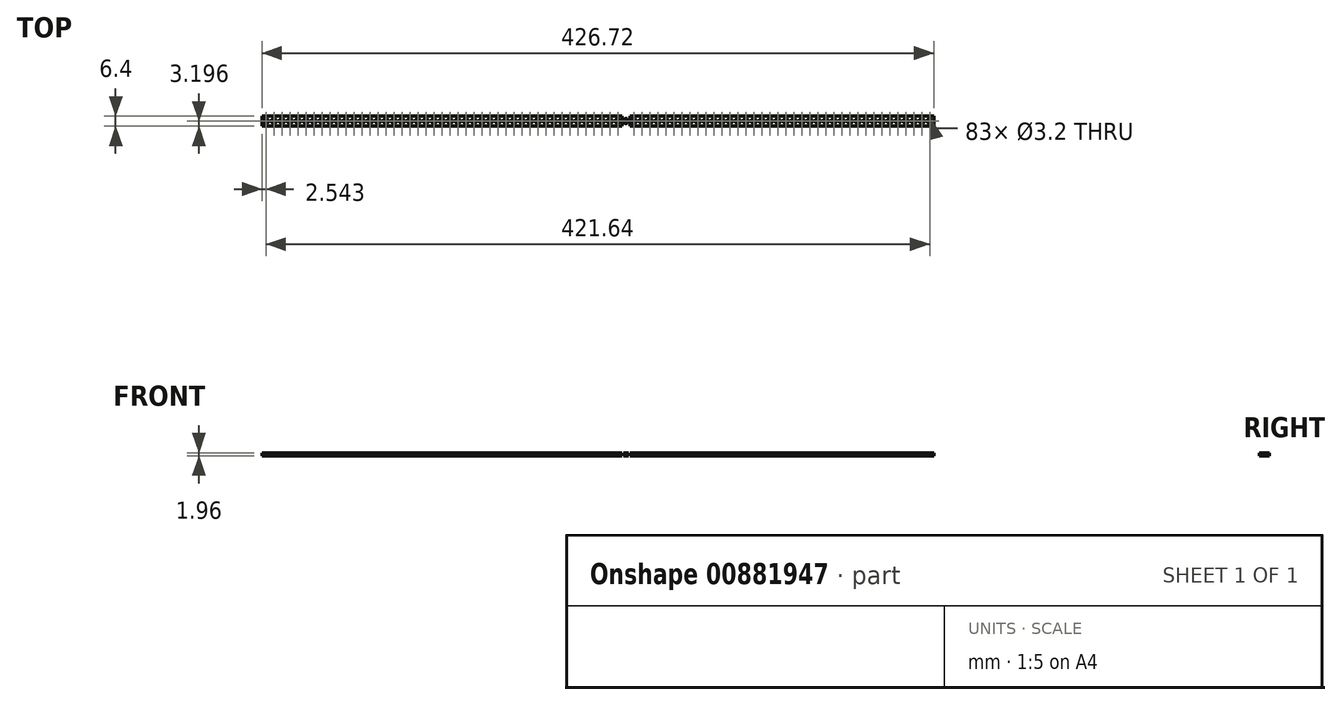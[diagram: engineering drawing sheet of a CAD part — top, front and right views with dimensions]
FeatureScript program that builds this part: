
annotation { "Feature Type Name" : "Feature", "Feature Type Description" : "" }
export const myFeature = defineFeature(function(context is Context, id is Id, definition is map)
    precondition{}
    {
        {
            var Q0;
            Q0=qCreatedBy(makeId("Top.planeOp"),FACE);
            var sketch = newSketch(context, id + "F0", { "sketchPlane" : qUnion([Q0])});
            skLineSegment(sketch, "E0.bottom", {"start": v(-207.84, -5.47) * mm, "end": v(218.88, -5.47) * mm});
            skLineSegment(sketch, "E0.top", {"start": v(-207.84, -11.87) * mm, "end": v(218.88, -11.87) * mm});
            skLineSegment(sketch, "E0.left", {"start": v(-207.84, -5.47) * mm, "end": v(-207.84, -11.87) * mm});
            skLineSegment(sketch, "E0.right", {"start": v(218.88, -5.47) * mm, "end": v(218.88, -11.87) * mm});
            skLineSegment(sketch, "E1.bottom", {"start": v(-207.84, -5.47) * mm, "end": v(-202.76, -5.47) * mm});
            skLineSegment(sketch, "E1.top", {"start": v(-207.84, -11.87) * mm, "end": v(-202.76, -11.87) * mm});
            skLineSegment(sketch, "E1.right", {"start": v(-202.76, -5.47) * mm, "end": v(-202.76, -11.87) * mm});
            skLineSegment(sketch, "E2.MirrorCS", {"start": v(-197.68, -5.47) * mm, "end": v(-197.68, -11.87) * mm});
            skLineSegment(sketch, "E3.MirrorCS", {"start": v(-192.6, -5.47) * mm, "end": v(-192.6, -11.87) * mm});
            skLineSegment(sketch, "E4.MirrorCS", {"start": v(-187.52, -5.47) * mm, "end": v(-187.52, -11.87) * mm});
            skLineSegment(sketch, "E5.MirrorCS", {"start": v(-182.44, -5.47) * mm, "end": v(-182.44, -11.87) * mm});
            skLineSegment(sketch, "E6.MirrorCS", {"start": v(-177.36, -5.47) * mm, "end": v(-177.36, -11.87) * mm});
            skLineSegment(sketch, "E7.MirrorCS", {"start": v(-172.28, -5.47) * mm, "end": v(-172.28, -11.87) * mm});
            skLineSegment(sketch, "E8.MirrorCS", {"start": v(-167.2, -5.47) * mm, "end": v(-167.2, -11.87) * mm});
            skCircle(sketch, "E9", {"center": v(-205.3, -8.67) * mm, "radius": 1.6 * mm});
            skCircle(sketch, "E10.MirrorC", {"center": v(-200.22, -8.67) * mm, "radius": 1.6 * mm});
            skCircle(sketch, "E11.MirrorC", {"center": v(-195.14, -8.67) * mm, "radius": 1.6 * mm});
            skCircle(sketch, "E12.MirrorC", {"center": v(-190.06, -8.67) * mm, "radius": 1.6 * mm});
            skCircle(sketch, "E13.MirrorC", {"center": v(-184.98, -8.67) * mm, "radius": 1.6 * mm});
            skCircle(sketch, "E14.MirrorC", {"center": v(-179.9, -8.67) * mm, "radius": 1.6 * mm});
            skCircle(sketch, "E15.MirrorC", {"center": v(-174.82, -8.67) * mm, "radius": 1.6 * mm});
            skCircle(sketch, "E16.MirrorC", {"center": v(-169.74, -8.67) * mm, "radius": 1.6 * mm});
            skCircle(sketch, "E17.MirrorC", {"center": v(-164.66, -8.67) * mm, "radius": 1.6 * mm});
            skLineSegment(sketch, "E18.MirrorCS", {"start": v(-162.12, -5.47) * mm, "end": v(-162.12, -11.87) * mm});
            skCircle(sketch, "E19.MirrorC", {"center": v(-159.58, -8.67) * mm, "radius": 1.6 * mm});
            skLineSegment(sketch, "E20.MirrorCS", {"start": v(-157.04, -5.47) * mm, "end": v(-157.04, -11.87) * mm});
            skCircle(sketch, "E21.MirrorC", {"center": v(-154.5, -8.67) * mm, "radius": 1.6 * mm});
            skLineSegment(sketch, "E22.MirrorCS", {"start": v(-151.96, -5.47) * mm, "end": v(-151.96, -11.87) * mm});
            skCircle(sketch, "E23.MirrorC", {"center": v(-149.42, -8.67) * mm, "radius": 1.6 * mm});
            skLineSegment(sketch, "E24.MirrorCS", {"start": v(-146.88, -5.47) * mm, "end": v(-146.88, -11.87) * mm});
            skCircle(sketch, "E25.MirrorC", {"center": v(-144.34, -8.67) * mm, "radius": 1.6 * mm});
            skLineSegment(sketch, "E26.MirrorCS", {"start": v(-141.8, -5.47) * mm, "end": v(-141.8, -11.87) * mm});
            skCircle(sketch, "E27.MirrorC", {"center": v(-139.26, -8.67) * mm, "radius": 1.6 * mm});
            skLineSegment(sketch, "E28.MirrorCS", {"start": v(-136.72, -5.47) * mm, "end": v(-136.72, -11.87) * mm});
            skCircle(sketch, "E29.MirrorC", {"center": v(-134.18, -8.67) * mm, "radius": 1.6 * mm});
            skLineSegment(sketch, "E30.MirrorCS", {"start": v(-131.64, -5.47) * mm, "end": v(-131.64, -11.87) * mm});
            skCircle(sketch, "E31.MirrorC", {"center": v(-129.1, -8.67) * mm, "radius": 1.6 * mm});
            skLineSegment(sketch, "E32.MirrorCS", {"start": v(-126.56, -5.47) * mm, "end": v(-126.56, -11.87) * mm});
            skCircle(sketch, "E33.MirrorC", {"center": v(-124.02, -8.67) * mm, "radius": 1.6 * mm});
            skLineSegment(sketch, "E34.MirrorCS", {"start": v(-121.48, -5.47) * mm, "end": v(-121.48, -11.87) * mm});
            skCircle(sketch, "E35.MirrorC", {"center": v(-118.94, -8.67) * mm, "radius": 1.6 * mm});
            skLineSegment(sketch, "E36.MirrorCS", {"start": v(-116.4, -5.47) * mm, "end": v(-116.4, -11.87) * mm});
            skCircle(sketch, "E37.MirrorC", {"center": v(-113.86, -8.67) * mm, "radius": 1.6 * mm});
            skLineSegment(sketch, "E38.MirrorCS", {"start": v(-111.32, -5.47) * mm, "end": v(-111.32, -11.87) * mm});
            skCircle(sketch, "E39.MirrorC", {"center": v(-108.78, -8.67) * mm, "radius": 1.6 * mm});
            skLineSegment(sketch, "E40.MirrorCS", {"start": v(-106.24, -5.47) * mm, "end": v(-106.24, -11.87) * mm});
            skCircle(sketch, "E41.MirrorC", {"center": v(-103.7, -8.67) * mm, "radius": 1.6 * mm});
            skLineSegment(sketch, "E42.MirrorCS", {"start": v(-101.16, -5.47) * mm, "end": v(-101.16, -11.87) * mm});
            skCircle(sketch, "E43.MirrorC", {"center": v(-98.62, -8.67) * mm, "radius": 1.6 * mm});
            skLineSegment(sketch, "E44.MirrorCS", {"start": v(-96.08, -5.47) * mm, "end": v(-96.08, -11.87) * mm});
            skCircle(sketch, "E45.MirrorC", {"center": v(-93.54, -8.67) * mm, "radius": 1.6 * mm});
            skLineSegment(sketch, "E46.MirrorCS", {"start": v(-91, -5.47) * mm, "end": v(-91, -11.87) * mm});
            skCircle(sketch, "E47.MirrorC", {"center": v(-88.46, -8.67) * mm, "radius": 1.6 * mm});
            skLineSegment(sketch, "E48.MirrorCS", {"start": v(-85.92, -5.47) * mm, "end": v(-85.92, -11.87) * mm});
            skCircle(sketch, "E49.MirrorC", {"center": v(-83.38, -8.67) * mm, "radius": 1.6 * mm});
            skLineSegment(sketch, "E50.MirrorCS", {"start": v(-80.84, -5.47) * mm, "end": v(-80.84, -11.87) * mm});
            skCircle(sketch, "E51.MirrorC", {"center": v(-78.3, -8.67) * mm, "radius": 1.6 * mm});
            skLineSegment(sketch, "E52.MirrorCS", {"start": v(-75.76, -5.47) * mm, "end": v(-75.76, -11.87) * mm});
            skCircle(sketch, "E53.MirrorC", {"center": v(-73.22, -8.67) * mm, "radius": 1.6 * mm});
            skLineSegment(sketch, "E54.MirrorCS", {"start": v(-70.68, -5.47) * mm, "end": v(-70.68, -11.87) * mm});
            skCircle(sketch, "E55.MirrorC", {"center": v(-68.14, -8.67) * mm, "radius": 1.6 * mm});
            skLineSegment(sketch, "E56.MirrorCS", {"start": v(-65.6, -5.47) * mm, "end": v(-65.6, -11.87) * mm});
            skCircle(sketch, "E57.MirrorC", {"center": v(-63.06, -8.67) * mm, "radius": 1.6 * mm});
            skLineSegment(sketch, "E58.MirrorCS", {"start": v(-60.52, -5.47) * mm, "end": v(-60.52, -11.87) * mm});
            skCircle(sketch, "E59.MirrorC", {"center": v(-57.98, -8.67) * mm, "radius": 1.6 * mm});
            skLineSegment(sketch, "E60.MirrorCS", {"start": v(-55.44, -5.47) * mm, "end": v(-55.44, -11.87) * mm});
            skCircle(sketch, "E61.MirrorC", {"center": v(-52.9, -8.67) * mm, "radius": 1.6 * mm});
            skLineSegment(sketch, "E62.MirrorCS", {"start": v(-50.36, -5.47) * mm, "end": v(-50.36, -11.87) * mm});
            skCircle(sketch, "E63.MirrorC", {"center": v(-47.82, -8.67) * mm, "radius": 1.6 * mm});
            skLineSegment(sketch, "E64.MirrorCS", {"start": v(-45.28, -5.47) * mm, "end": v(-45.28, -11.87) * mm});
            skCircle(sketch, "E65.MirrorC", {"center": v(-42.74, -8.67) * mm, "radius": 1.6 * mm});
            skLineSegment(sketch, "E66.MirrorCS", {"start": v(-40.2, -5.47) * mm, "end": v(-40.2, -11.87) * mm});
            skCircle(sketch, "E67.MirrorC", {"center": v(-37.66, -8.67) * mm, "radius": 1.6 * mm});
            skLineSegment(sketch, "E68.MirrorCS", {"start": v(-35.12, -5.47) * mm, "end": v(-35.12, -11.87) * mm});
            skCircle(sketch, "E69.MirrorC", {"center": v(-32.58, -8.67) * mm, "radius": 1.6 * mm});
            skLineSegment(sketch, "E70.MirrorCS", {"start": v(-30.04, -5.47) * mm, "end": v(-30.04, -11.87) * mm});
            skCircle(sketch, "E71.MirrorC", {"center": v(-27.5, -8.67) * mm, "radius": 1.6 * mm});
            skLineSegment(sketch, "E72.MirrorCS", {"start": v(-24.96, -5.47) * mm, "end": v(-24.96, -11.87) * mm});
            skLineSegment(sketch, "E73.MirrorCS", {"start": v(-19.88, -5.47) * mm, "end": v(-19.88, -11.87) * mm});
            skCircle(sketch, "E74.MirrorC", {"center": v(-17.34, -8.67) * mm, "radius": 1.6 * mm});
            skLineSegment(sketch, "E75.MirrorCS", {"start": v(-14.8, -5.47) * mm, "end": v(-14.8, -11.87) * mm});
            skCircle(sketch, "E76.MirrorC", {"center": v(-12.26, -8.67) * mm, "radius": 1.6 * mm});
            skLineSegment(sketch, "E77.MirrorCS", {"start": v(-9.72, -5.47) * mm, "end": v(-9.72, -11.87) * mm});
            skCircle(sketch, "E78.MirrorC", {"center": v(-7.18, -8.67) * mm, "radius": 1.6 * mm});
            skLineSegment(sketch, "E79.MirrorCS", {"start": v(-4.64, -5.47) * mm, "end": v(-4.64, -11.87) * mm});
            skCircle(sketch, "E80.MirrorC", {"center": v(-2.1, -8.67) * mm, "radius": 1.6 * mm});
            skCircle(sketch, "E81.MirrorC", {"center": v(-22.42, -8.67) * mm, "radius": 1.6 * mm});
            skLineSegment(sketch, "E82.MirrorCS", {"start": v(0.44, -5.47) * mm, "end": v(0.44, -11.87) * mm});
            skCircle(sketch, "E83.MirrorC", {"center": v(2.98, -8.67) * mm, "radius": 1.6 * mm});
            skLineSegment(sketch, "E84.MirrorCS", {"start": v(5.52, -5.47) * mm, "end": v(5.52, -11.87) * mm});
            skLineSegment(sketch, "E85.MirrorCS", {"start": v(10.6, -5.47) * mm, "end": v(10.6, -11.87) * mm});
            skCircle(sketch, "E86.MirrorC", {"center": v(13.14, -8.67) * mm, "radius": 1.6 * mm});
            skCircle(sketch, "E87.MirrorC", {"center": v(8.06, -8.67) * mm, "radius": 1.6 * mm});
            skLineSegment(sketch, "E88.MirrorCS", {"start": v(15.68, -5.47) * mm, "end": v(15.68, -11.87) * mm});
            skCircle(sketch, "E89.MirrorC", {"center": v(18.22, -8.67) * mm, "radius": 1.6 * mm});
            skCircle(sketch, "E90.MirrorC", {"center": v(23.3, -8.67) * mm, "radius": 1.6 * mm});
            skLineSegment(sketch, "E91.MirrorCS", {"start": v(20.76, -5.47) * mm, "end": v(20.76, -11.87) * mm});
            skLineSegment(sketch, "E92.MirrorCS", {"start": v(25.84, -5.47) * mm, "end": v(25.84, -11.87) * mm});
            skCircle(sketch, "E93.MirrorC", {"center": v(28.38, -8.67) * mm, "radius": 1.6 * mm});
            skLineSegment(sketch, "E94.MirrorCS", {"start": v(30.92, -5.47) * mm, "end": v(30.92, -11.87) * mm});
            skCircle(sketch, "E95.MirrorC", {"center": v(33.46, -8.67) * mm, "radius": 1.6 * mm});
            skLineSegment(sketch, "E96.MirrorCS", {"start": v(36, -5.47) * mm, "end": v(36, -11.87) * mm});
            skCircle(sketch, "E97.MirrorC", {"center": v(38.54, -8.67) * mm, "radius": 1.6 * mm});
            skLineSegment(sketch, "E98.MirrorCS", {"start": v(41.08, -5.47) * mm, "end": v(41.08, -11.87) * mm});
            skCircle(sketch, "E99.MirrorC", {"center": v(43.62, -8.67) * mm, "radius": 1.6 * mm});
            skLineSegment(sketch, "E100.MirrorCS", {"start": v(46.16, -5.47) * mm, "end": v(46.16, -11.87) * mm});
            skCircle(sketch, "E101.MirrorC", {"center": v(48.7, -8.67) * mm, "radius": 1.6 * mm});
            skLineSegment(sketch, "E102.MirrorCS", {"start": v(51.24, -5.47) * mm, "end": v(51.24, -11.87) * mm});
            skCircle(sketch, "E103.MirrorC", {"center": v(53.78, -8.67) * mm, "radius": 1.6 * mm});
            skLineSegment(sketch, "E104.MirrorCS", {"start": v(56.32, -5.47) * mm, "end": v(56.32, -11.87) * mm});
            skCircle(sketch, "E105.MirrorC", {"center": v(58.86, -8.67) * mm, "radius": 1.6 * mm});
            skLineSegment(sketch, "E106.MirrorCS", {"start": v(61.4, -5.47) * mm, "end": v(61.4, -11.87) * mm});
            skCircle(sketch, "E107.MirrorC", {"center": v(63.94, -8.67) * mm, "radius": 1.6 * mm});
            skLineSegment(sketch, "E108.MirrorCS", {"start": v(66.48, -5.47) * mm, "end": v(66.48, -11.87) * mm});
            skCircle(sketch, "E109.MirrorC", {"center": v(69.02, -8.67) * mm, "radius": 1.6 * mm});
            skLineSegment(sketch, "E110.MirrorCS", {"start": v(71.56, -5.47) * mm, "end": v(71.56, -11.87) * mm});
            skCircle(sketch, "E111.MirrorC", {"center": v(74.1, -8.67) * mm, "radius": 1.6 * mm});
            skLineSegment(sketch, "E112.MirrorCS", {"start": v(76.64, -5.47) * mm, "end": v(76.64, -11.87) * mm});
            skCircle(sketch, "E113.MirrorC", {"center": v(79.18, -8.67) * mm, "radius": 1.6 * mm});
            skLineSegment(sketch, "E114.MirrorCS", {"start": v(81.72, -5.47) * mm, "end": v(81.72, -11.87) * mm});
            skCircle(sketch, "E115.MirrorC", {"center": v(84.26, -8.67) * mm, "radius": 1.6 * mm});
            skLineSegment(sketch, "E116.MirrorCS", {"start": v(86.8, -5.47) * mm, "end": v(86.8, -11.87) * mm});
            skCircle(sketch, "E117.MirrorC", {"center": v(89.34, -8.67) * mm, "radius": 1.6 * mm});
            skLineSegment(sketch, "E118.MirrorCS", {"start": v(91.88, -5.47) * mm, "end": v(91.88, -11.87) * mm});
            skCircle(sketch, "E119.MirrorC", {"center": v(94.42, -8.67) * mm, "radius": 1.6 * mm});
            skLineSegment(sketch, "E120.MirrorCS", {"start": v(96.96, -5.47) * mm, "end": v(96.96, -11.87) * mm});
            skCircle(sketch, "E121.MirrorC", {"center": v(99.5, -8.67) * mm, "radius": 1.6 * mm});
            skLineSegment(sketch, "E122.MirrorCS", {"start": v(102.04, -5.47) * mm, "end": v(102.04, -11.87) * mm});
            skCircle(sketch, "E123.MirrorC", {"center": v(104.58, -8.67) * mm, "radius": 1.6 * mm});
            skLineSegment(sketch, "E124.MirrorCS", {"start": v(107.12, -5.47) * mm, "end": v(107.12, -11.87) * mm});
            skCircle(sketch, "E125.MirrorC", {"center": v(109.66, -8.67) * mm, "radius": 1.6 * mm});
            skLineSegment(sketch, "E126.MirrorCS", {"start": v(112.2, -5.47) * mm, "end": v(112.2, -11.87) * mm});
            skCircle(sketch, "E127.MirrorC", {"center": v(114.74, -8.67) * mm, "radius": 1.6 * mm});
            skLineSegment(sketch, "E128.MirrorCS", {"start": v(117.28, -5.47) * mm, "end": v(117.28, -11.87) * mm});
            skCircle(sketch, "E129.MirrorC", {"center": v(119.82, -8.67) * mm, "radius": 1.6 * mm});
            skLineSegment(sketch, "E130.MirrorCS", {"start": v(122.36, -5.47) * mm, "end": v(122.36, -11.87) * mm});
            skCircle(sketch, "E131.MirrorC", {"center": v(124.9, -8.67) * mm, "radius": 1.6 * mm});
            skLineSegment(sketch, "E132.MirrorCS", {"start": v(127.44, -5.47) * mm, "end": v(127.44, -11.87) * mm});
            skCircle(sketch, "E133.MirrorC", {"center": v(129.98, -8.67) * mm, "radius": 1.6 * mm});
            skLineSegment(sketch, "E134.MirrorCS", {"start": v(132.52, -5.47) * mm, "end": v(132.52, -11.87) * mm});
            skCircle(sketch, "E135.MirrorC", {"center": v(135.06, -8.67) * mm, "radius": 1.6 * mm});
            skLineSegment(sketch, "E136.MirrorCS", {"start": v(137.6, -5.47) * mm, "end": v(137.6, -11.87) * mm});
            skCircle(sketch, "E137.MirrorC", {"center": v(140.14, -8.67) * mm, "radius": 1.6 * mm});
            skLineSegment(sketch, "E138.MirrorCS", {"start": v(142.68, -5.47) * mm, "end": v(142.68, -11.87) * mm});
            skCircle(sketch, "E139.MirrorC", {"center": v(145.22, -8.67) * mm, "radius": 1.6 * mm});
            skLineSegment(sketch, "E140.MirrorCS", {"start": v(147.76, -5.47) * mm, "end": v(147.76, -11.87) * mm});
            skCircle(sketch, "E141.MirrorC", {"center": v(150.3, -8.67) * mm, "radius": 1.6 * mm});
            skLineSegment(sketch, "E142.MirrorCS", {"start": v(152.84, -5.47) * mm, "end": v(152.84, -11.87) * mm});
            skCircle(sketch, "E143.MirrorC", {"center": v(155.38, -8.67) * mm, "radius": 1.6 * mm});
            skLineSegment(sketch, "E144.MirrorCS", {"start": v(157.92, -5.47) * mm, "end": v(157.92, -11.87) * mm});
            skCircle(sketch, "E145.MirrorC", {"center": v(160.46, -8.67) * mm, "radius": 1.6 * mm});
            skLineSegment(sketch, "E146.MirrorCS", {"start": v(163, -5.47) * mm, "end": v(163, -11.87) * mm});
            skCircle(sketch, "E147.MirrorC", {"center": v(165.54, -8.67) * mm, "radius": 1.6 * mm});
            skLineSegment(sketch, "E148.MirrorCS", {"start": v(168.08, -5.47) * mm, "end": v(168.08, -11.87) * mm});
            skCircle(sketch, "E149.MirrorC", {"center": v(170.62, -8.67) * mm, "radius": 1.6 * mm});
            skLineSegment(sketch, "E150.MirrorCS", {"start": v(173.16, -5.47) * mm, "end": v(173.16, -11.87) * mm});
            skCircle(sketch, "E151.MirrorC", {"center": v(175.7, -8.67) * mm, "radius": 1.6 * mm});
            skLineSegment(sketch, "E152.MirrorCS", {"start": v(178.24, -5.47) * mm, "end": v(178.24, -11.87) * mm});
            skCircle(sketch, "E153.MirrorC", {"center": v(180.78, -8.67) * mm, "radius": 1.6 * mm});
            skLineSegment(sketch, "E154.MirrorCS", {"start": v(183.32, -5.47) * mm, "end": v(183.32, -11.87) * mm});
            skCircle(sketch, "E155.MirrorC", {"center": v(185.86, -8.67) * mm, "radius": 1.6 * mm});
            skLineSegment(sketch, "E156.MirrorCS", {"start": v(188.4, -5.47) * mm, "end": v(188.4, -11.87) * mm});
            skCircle(sketch, "E157.MirrorC", {"center": v(190.94, -8.67) * mm, "radius": 1.6 * mm});
            skLineSegment(sketch, "E158.MirrorCS", {"start": v(193.48, -5.47) * mm, "end": v(193.48, -11.87) * mm});
            skCircle(sketch, "E159.MirrorC", {"center": v(196.02, -8.67) * mm, "radius": 1.6 * mm});
            skLineSegment(sketch, "E160.MirrorCS", {"start": v(198.56, -5.47) * mm, "end": v(198.56, -11.87) * mm});
            skCircle(sketch, "E161.MirrorC", {"center": v(201.1, -8.67) * mm, "radius": 1.6 * mm});
            skLineSegment(sketch, "E162.MirrorCS", {"start": v(203.64, -5.47) * mm, "end": v(203.64, -11.87) * mm});
            skCircle(sketch, "E163.MirrorC", {"center": v(206.18, -8.67) * mm, "radius": 1.6 * mm});
            skLineSegment(sketch, "E164.MirrorCS", {"start": v(208.72, -5.47) * mm, "end": v(208.72, -11.87) * mm});
            skCircle(sketch, "E165.MirrorC", {"center": v(211.26, -8.67) * mm, "radius": 1.6 * mm});
            skLineSegment(sketch, "E166.MirrorCS", {"start": v(213.8, -5.47) * mm, "end": v(213.8, -11.87) * mm});
            skCircle(sketch, "E167.MirrorC", {"center": v(216.34, -8.67) * mm, "radius": 1.6 * mm});
            skSolve(sketch);
        }
        {
            var Q0;
            {var subQ1=sQuery(id+"F0.wireOp",EDGE,"E0.left");Q0=makeQuery(id+"F0.imprint","IMPRINT",FACE,{"disambiguationData":[TD([[makeQuery(id+"F0.imprint","IMPRINT",EDGE,{"derivedFrom":subQ1}),1.0]])]});}
            var Q1;
            {var subQ1=sQuery(id+"F0.wireOp",EDGE,"E1.right");Q1=makeQuery(id+"F0.imprint","IMPRINT",FACE,{"disambiguationData":[TD([[makeQuery(id+"F0.imprint","IMPRINT",EDGE,{"derivedFrom":subQ1}),1.0]])]});}
            var Q2;
            {var subQ1=sQuery(id+"F0.wireOp",EDGE,"E2.MirrorCS");Q2=makeQuery(id+"F0.imprint","IMPRINT",FACE,{"disambiguationData":[TD([[makeQuery(id+"F0.imprint","IMPRINT",EDGE,{"derivedFrom":subQ1}),1.0]])]});}
            var Q3;
            {var subQ0=sQuery(id+"F0.wireOp",EDGE,"E3.MirrorCS");Q3=makeQuery(id+"F0.imprint","IMPRINT",FACE,{"disambiguationData":[TD([[makeQuery(id+"F0.imprint","IMPRINT",EDGE,{"derivedFrom":subQ0}),1.0]])]});}
            var Q4;
            {var subQ1=sQuery(id+"F0.wireOp",EDGE,"E4.MirrorCS");Q4=makeQuery(id+"F0.imprint","IMPRINT",FACE,{"disambiguationData":[TD([[makeQuery(id+"F0.imprint","IMPRINT",EDGE,{"derivedFrom":subQ1}),1.0]])]});}
            var Q5;
            {var subQ1=sQuery(id+"F0.wireOp",EDGE,"E5.MirrorCS");Q5=makeQuery(id+"F0.imprint","IMPRINT",FACE,{"disambiguationData":[TD([[makeQuery(id+"F0.imprint","IMPRINT",EDGE,{"derivedFrom":subQ1}),1.0]])]});}
            var Q6;
            {var subQ1=sQuery(id+"F0.wireOp",EDGE,"E6.MirrorCS");Q6=makeQuery(id+"F0.imprint","IMPRINT",FACE,{"disambiguationData":[TD([[makeQuery(id+"F0.imprint","IMPRINT",EDGE,{"derivedFrom":subQ1}),1.0]])]});}
            var Q7;
            {var subQ1=sQuery(id+"F0.wireOp",EDGE,"E7.MirrorCS");Q7=makeQuery(id+"F0.imprint","IMPRINT",FACE,{"disambiguationData":[TD([[makeQuery(id+"F0.imprint","IMPRINT",EDGE,{"derivedFrom":subQ1}),1.0]])]});}
            var Q8;
            {var subQ0=sQuery(id+"F0.wireOp",EDGE,"E8.MirrorCS");Q8=makeQuery(id+"F0.imprint","IMPRINT",FACE,{"disambiguationData":[TD([[makeQuery(id+"F0.imprint","IMPRINT",EDGE,{"derivedFrom":subQ0}),1.0]])]});}
            var Q9;
            {var subQ0=sQuery(id+"F0.wireOp",EDGE,"E18.MirrorCS");Q9=makeQuery(id+"F0.imprint","IMPRINT",FACE,{"disambiguationData":[TD([[makeQuery(id+"F0.imprint","IMPRINT",EDGE,{"derivedFrom":subQ0}),1.0]])]});}
            var Q10;
            {var subQ0=sQuery(id+"F0.wireOp",EDGE,"E20.MirrorCS");Q10=makeQuery(id+"F0.imprint","IMPRINT",FACE,{"disambiguationData":[TD([[makeQuery(id+"F0.imprint","IMPRINT",EDGE,{"derivedFrom":subQ0}),1.0]])]});}
            var Q11;
            {var subQ0=sQuery(id+"F0.wireOp",EDGE,"E22.MirrorCS");Q11=makeQuery(id+"F0.imprint","IMPRINT",FACE,{"disambiguationData":[TD([[makeQuery(id+"F0.imprint","IMPRINT",EDGE,{"derivedFrom":subQ0}),1.0]])]});}
            var Q12;
            {var subQ0=sQuery(id+"F0.wireOp",EDGE,"E24.MirrorCS");Q12=makeQuery(id+"F0.imprint","IMPRINT",FACE,{"disambiguationData":[TD([[makeQuery(id+"F0.imprint","IMPRINT",EDGE,{"derivedFrom":subQ0}),1.0]])]});}
            var Q13;
            {var subQ0=sQuery(id+"F0.wireOp",EDGE,"E26.MirrorCS");Q13=makeQuery(id+"F0.imprint","IMPRINT",FACE,{"disambiguationData":[TD([[makeQuery(id+"F0.imprint","IMPRINT",EDGE,{"derivedFrom":subQ0}),1.0]])]});}
            var Q14;
            {var subQ0=sQuery(id+"F0.wireOp",EDGE,"E28.MirrorCS");Q14=makeQuery(id+"F0.imprint","IMPRINT",FACE,{"disambiguationData":[TD([[makeQuery(id+"F0.imprint","IMPRINT",EDGE,{"derivedFrom":subQ0}),1.0]])]});}
            var Q15;
            {var subQ0=sQuery(id+"F0.wireOp",EDGE,"E30.MirrorCS");Q15=makeQuery(id+"F0.imprint","IMPRINT",FACE,{"disambiguationData":[TD([[makeQuery(id+"F0.imprint","IMPRINT",EDGE,{"derivedFrom":subQ0}),1.0]])]});}
            var Q16;
            {var subQ0=sQuery(id+"F0.wireOp",EDGE,"E32.MirrorCS");Q16=makeQuery(id+"F0.imprint","IMPRINT",FACE,{"disambiguationData":[TD([[makeQuery(id+"F0.imprint","IMPRINT",EDGE,{"derivedFrom":subQ0}),1.0]])]});}
            var Q17;
            {var subQ0=sQuery(id+"F0.wireOp",EDGE,"E34.MirrorCS");Q17=makeQuery(id+"F0.imprint","IMPRINT",FACE,{"disambiguationData":[TD([[makeQuery(id+"F0.imprint","IMPRINT",EDGE,{"derivedFrom":subQ0}),1.0]])]});}
            var Q18;
            {var subQ0=sQuery(id+"F0.wireOp",EDGE,"E36.MirrorCS");Q18=makeQuery(id+"F0.imprint","IMPRINT",FACE,{"disambiguationData":[TD([[makeQuery(id+"F0.imprint","IMPRINT",EDGE,{"derivedFrom":subQ0}),1.0]])]});}
            var Q19;
            {var subQ0=sQuery(id+"F0.wireOp",EDGE,"E38.MirrorCS");Q19=makeQuery(id+"F0.imprint","IMPRINT",FACE,{"disambiguationData":[TD([[makeQuery(id+"F0.imprint","IMPRINT",EDGE,{"derivedFrom":subQ0}),1.0]])]});}
            var Q20;
            {var subQ0=sQuery(id+"F0.wireOp",EDGE,"E40.MirrorCS");Q20=makeQuery(id+"F0.imprint","IMPRINT",FACE,{"disambiguationData":[TD([[makeQuery(id+"F0.imprint","IMPRINT",EDGE,{"derivedFrom":subQ0}),1.0]])]});}
            var Q21;
            {var subQ0=sQuery(id+"F0.wireOp",EDGE,"E42.MirrorCS");Q21=makeQuery(id+"F0.imprint","IMPRINT",FACE,{"disambiguationData":[TD([[makeQuery(id+"F0.imprint","IMPRINT",EDGE,{"derivedFrom":subQ0}),1.0]])]});}
            var Q22;
            {var subQ0=sQuery(id+"F0.wireOp",EDGE,"E44.MirrorCS");Q22=makeQuery(id+"F0.imprint","IMPRINT",FACE,{"disambiguationData":[TD([[makeQuery(id+"F0.imprint","IMPRINT",EDGE,{"derivedFrom":subQ0}),1.0]])]});}
            var Q23;
            {var subQ0=sQuery(id+"F0.wireOp",EDGE,"E46.MirrorCS");Q23=makeQuery(id+"F0.imprint","IMPRINT",FACE,{"disambiguationData":[TD([[makeQuery(id+"F0.imprint","IMPRINT",EDGE,{"derivedFrom":subQ0}),1.0]])]});}
            var Q24;
            {var subQ0=sQuery(id+"F0.wireOp",EDGE,"E48.MirrorCS");Q24=makeQuery(id+"F0.imprint","IMPRINT",FACE,{"disambiguationData":[TD([[makeQuery(id+"F0.imprint","IMPRINT",EDGE,{"derivedFrom":subQ0}),1.0]])]});}
            var Q25;
            {var subQ0=sQuery(id+"F0.wireOp",EDGE,"E50.MirrorCS");Q25=makeQuery(id+"F0.imprint","IMPRINT",FACE,{"disambiguationData":[TD([[makeQuery(id+"F0.imprint","IMPRINT",EDGE,{"derivedFrom":subQ0}),1.0]])]});}
            var Q26;
            {var subQ0=sQuery(id+"F0.wireOp",EDGE,"E52.MirrorCS");Q26=makeQuery(id+"F0.imprint","IMPRINT",FACE,{"disambiguationData":[TD([[makeQuery(id+"F0.imprint","IMPRINT",EDGE,{"derivedFrom":subQ0}),1.0]])]});}
            var Q27;
            {var subQ0=sQuery(id+"F0.wireOp",EDGE,"E54.MirrorCS");Q27=makeQuery(id+"F0.imprint","IMPRINT",FACE,{"disambiguationData":[TD([[makeQuery(id+"F0.imprint","IMPRINT",EDGE,{"derivedFrom":subQ0}),1.0]])]});}
            var Q28;
            {var subQ0=sQuery(id+"F0.wireOp",EDGE,"E56.MirrorCS");Q28=makeQuery(id+"F0.imprint","IMPRINT",FACE,{"disambiguationData":[TD([[makeQuery(id+"F0.imprint","IMPRINT",EDGE,{"derivedFrom":subQ0}),1.0]])]});}
            var Q29;
            {var subQ0=sQuery(id+"F0.wireOp",EDGE,"E58.MirrorCS");Q29=makeQuery(id+"F0.imprint","IMPRINT",FACE,{"disambiguationData":[TD([[makeQuery(id+"F0.imprint","IMPRINT",EDGE,{"derivedFrom":subQ0}),1.0]])]});}
            var Q30;
            {var subQ0=sQuery(id+"F0.wireOp",EDGE,"E60.MirrorCS");Q30=makeQuery(id+"F0.imprint","IMPRINT",FACE,{"disambiguationData":[TD([[makeQuery(id+"F0.imprint","IMPRINT",EDGE,{"derivedFrom":subQ0}),1.0]])]});}
            var Q31;
            {var subQ0=sQuery(id+"F0.wireOp",EDGE,"E62.MirrorCS");Q31=makeQuery(id+"F0.imprint","IMPRINT",FACE,{"disambiguationData":[TD([[makeQuery(id+"F0.imprint","IMPRINT",EDGE,{"derivedFrom":subQ0}),1.0]])]});}
            var Q32;
            {var subQ0=sQuery(id+"F0.wireOp",EDGE,"E64.MirrorCS");Q32=makeQuery(id+"F0.imprint","IMPRINT",FACE,{"disambiguationData":[TD([[makeQuery(id+"F0.imprint","IMPRINT",EDGE,{"derivedFrom":subQ0}),1.0]])]});}
            var Q33;
            {var subQ0=sQuery(id+"F0.wireOp",EDGE,"E66.MirrorCS");Q33=makeQuery(id+"F0.imprint","IMPRINT",FACE,{"disambiguationData":[TD([[makeQuery(id+"F0.imprint","IMPRINT",EDGE,{"derivedFrom":subQ0}),1.0]])]});}
            var Q34;
            {var subQ0=sQuery(id+"F0.wireOp",EDGE,"E68.MirrorCS");Q34=makeQuery(id+"F0.imprint","IMPRINT",FACE,{"disambiguationData":[TD([[makeQuery(id+"F0.imprint","IMPRINT",EDGE,{"derivedFrom":subQ0}),1.0]])]});}
            var Q35;
            {var subQ0=sQuery(id+"F0.wireOp",EDGE,"E70.MirrorCS");Q35=makeQuery(id+"F0.imprint","IMPRINT",FACE,{"disambiguationData":[TD([[makeQuery(id+"F0.imprint","IMPRINT",EDGE,{"derivedFrom":subQ0}),1.0]])]});}
            var Q36;
            {var subQ1=sQuery(id+"F0.wireOp",EDGE,"E72.MirrorCS");Q36=makeQuery(id+"F0.imprint","IMPRINT",FACE,{"disambiguationData":[TD([[makeQuery(id+"F0.imprint","IMPRINT",EDGE,{"derivedFrom":subQ1}),1.0]])]});}
            var Q37;
            {var subQ0=sQuery(id+"F0.wireOp",EDGE,"E73.MirrorCS");Q37=makeQuery(id+"F0.imprint","IMPRINT",FACE,{"disambiguationData":[TD([[makeQuery(id+"F0.imprint","IMPRINT",EDGE,{"derivedFrom":subQ0}),1.0]])]});}
            var Q38;
            {var subQ0=sQuery(id+"F0.wireOp",EDGE,"E75.MirrorCS");Q38=makeQuery(id+"F0.imprint","IMPRINT",FACE,{"disambiguationData":[TD([[makeQuery(id+"F0.imprint","IMPRINT",EDGE,{"derivedFrom":subQ0}),1.0]])]});}
            var Q39;
            {var subQ0=sQuery(id+"F0.wireOp",EDGE,"E77.MirrorCS");Q39=makeQuery(id+"F0.imprint","IMPRINT",FACE,{"disambiguationData":[TD([[makeQuery(id+"F0.imprint","IMPRINT",EDGE,{"derivedFrom":subQ0}),1.0]])]});}
            var Q40;
            {var subQ0=sQuery(id+"F0.wireOp",EDGE,"E79.MirrorCS");Q40=makeQuery(id+"F0.imprint","IMPRINT",FACE,{"disambiguationData":[TD([[makeQuery(id+"F0.imprint","IMPRINT",EDGE,{"derivedFrom":subQ0}),1.0]])]});}
            var Q41;
            {var subQ0=sQuery(id+"F0.wireOp",EDGE,"E82.MirrorCS");Q41=makeQuery(id+"F0.imprint","IMPRINT",FACE,{"disambiguationData":[TD([[makeQuery(id+"F0.imprint","IMPRINT",EDGE,{"derivedFrom":subQ0}),1.0]])]});}
            var Q42;
            {var subQ1=sQuery(id+"F0.wireOp",EDGE,"E84.MirrorCS");Q42=makeQuery(id+"F0.imprint","IMPRINT",FACE,{"disambiguationData":[TD([[makeQuery(id+"F0.imprint","IMPRINT",EDGE,{"derivedFrom":subQ1}),1.0]])]});}
            var Q43;
            {var subQ0=sQuery(id+"F0.wireOp",EDGE,"E85.MirrorCS");Q43=makeQuery(id+"F0.imprint","IMPRINT",FACE,{"disambiguationData":[TD([[makeQuery(id+"F0.imprint","IMPRINT",EDGE,{"derivedFrom":subQ0}),1.0]])]});}
            var Q44;
            {var subQ0=sQuery(id+"F0.wireOp",EDGE,"E88.MirrorCS");Q44=makeQuery(id+"F0.imprint","IMPRINT",FACE,{"disambiguationData":[TD([[makeQuery(id+"F0.imprint","IMPRINT",EDGE,{"derivedFrom":subQ0}),1.0]])]});}
            var Q45;
            Q45=makeQuery(id+"F0.imprint","IMPRINT",FACE,{"disambiguationData":[TD([[makeQuery(id+"F0.imprint","IMPRINT",EDGE,{"derivedFrom":sQuery(id+"F0.wireOp",EDGE,"E90.MirrorC")}),1.0]])]});
            var Q46;
            {var subQ0=sQuery(id+"F0.wireOp",EDGE,"E92.MirrorCS");Q46=makeQuery(id+"F0.imprint","IMPRINT",FACE,{"disambiguationData":[TD([[makeQuery(id+"F0.imprint","IMPRINT",EDGE,{"derivedFrom":subQ0}),1.0]])]});}
            var Q47;
            {var subQ0=sQuery(id+"F0.wireOp",EDGE,"E94.MirrorCS");Q47=makeQuery(id+"F0.imprint","IMPRINT",FACE,{"disambiguationData":[TD([[makeQuery(id+"F0.imprint","IMPRINT",EDGE,{"derivedFrom":subQ0}),1.0]])]});}
            var Q48;
            {var subQ0=sQuery(id+"F0.wireOp",EDGE,"E96.MirrorCS");Q48=makeQuery(id+"F0.imprint","IMPRINT",FACE,{"disambiguationData":[TD([[makeQuery(id+"F0.imprint","IMPRINT",EDGE,{"derivedFrom":subQ0}),1.0]])]});}
            var Q49;
            {var subQ0=sQuery(id+"F0.wireOp",EDGE,"E98.MirrorCS");Q49=makeQuery(id+"F0.imprint","IMPRINT",FACE,{"disambiguationData":[TD([[makeQuery(id+"F0.imprint","IMPRINT",EDGE,{"derivedFrom":subQ0}),1.0]])]});}
            var Q50;
            {var subQ0=sQuery(id+"F0.wireOp",EDGE,"E100.MirrorCS");Q50=makeQuery(id+"F0.imprint","IMPRINT",FACE,{"disambiguationData":[TD([[makeQuery(id+"F0.imprint","IMPRINT",EDGE,{"derivedFrom":subQ0}),1.0]])]});}
            var Q51;
            {var subQ0=sQuery(id+"F0.wireOp",EDGE,"E102.MirrorCS");Q51=makeQuery(id+"F0.imprint","IMPRINT",FACE,{"disambiguationData":[TD([[makeQuery(id+"F0.imprint","IMPRINT",EDGE,{"derivedFrom":subQ0}),1.0]])]});}
            var Q52;
            {var subQ0=sQuery(id+"F0.wireOp",EDGE,"E104.MirrorCS");Q52=makeQuery(id+"F0.imprint","IMPRINT",FACE,{"disambiguationData":[TD([[makeQuery(id+"F0.imprint","IMPRINT",EDGE,{"derivedFrom":subQ0}),1.0]])]});}
            var Q53;
            {var subQ0=sQuery(id+"F0.wireOp",EDGE,"E106.MirrorCS");Q53=makeQuery(id+"F0.imprint","IMPRINT",FACE,{"disambiguationData":[TD([[makeQuery(id+"F0.imprint","IMPRINT",EDGE,{"derivedFrom":subQ0}),1.0]])]});}
            var Q54;
            {var subQ0=sQuery(id+"F0.wireOp",EDGE,"E108.MirrorCS");Q54=makeQuery(id+"F0.imprint","IMPRINT",FACE,{"disambiguationData":[TD([[makeQuery(id+"F0.imprint","IMPRINT",EDGE,{"derivedFrom":subQ0}),1.0]])]});}
            var Q55;
            {var subQ0=sQuery(id+"F0.wireOp",EDGE,"E110.MirrorCS");Q55=makeQuery(id+"F0.imprint","IMPRINT",FACE,{"disambiguationData":[TD([[makeQuery(id+"F0.imprint","IMPRINT",EDGE,{"derivedFrom":subQ0}),1.0]])]});}
            var Q56;
            {var subQ0=sQuery(id+"F0.wireOp",EDGE,"E112.MirrorCS");Q56=makeQuery(id+"F0.imprint","IMPRINT",FACE,{"disambiguationData":[TD([[makeQuery(id+"F0.imprint","IMPRINT",EDGE,{"derivedFrom":subQ0}),1.0]])]});}
            var Q57;
            {var subQ0=sQuery(id+"F0.wireOp",EDGE,"E114.MirrorCS");Q57=makeQuery(id+"F0.imprint","IMPRINT",FACE,{"disambiguationData":[TD([[makeQuery(id+"F0.imprint","IMPRINT",EDGE,{"derivedFrom":subQ0}),1.0]])]});}
            var Q58;
            {var subQ0=sQuery(id+"F0.wireOp",EDGE,"E116.MirrorCS");Q58=makeQuery(id+"F0.imprint","IMPRINT",FACE,{"disambiguationData":[TD([[makeQuery(id+"F0.imprint","IMPRINT",EDGE,{"derivedFrom":subQ0}),1.0]])]});}
            var Q59;
            {var subQ0=sQuery(id+"F0.wireOp",EDGE,"E118.MirrorCS");Q59=makeQuery(id+"F0.imprint","IMPRINT",FACE,{"disambiguationData":[TD([[makeQuery(id+"F0.imprint","IMPRINT",EDGE,{"derivedFrom":subQ0}),1.0]])]});}
            var Q60;
            {var subQ0=sQuery(id+"F0.wireOp",EDGE,"E120.MirrorCS");Q60=makeQuery(id+"F0.imprint","IMPRINT",FACE,{"disambiguationData":[TD([[makeQuery(id+"F0.imprint","IMPRINT",EDGE,{"derivedFrom":subQ0}),1.0]])]});}
            var Q61;
            {var subQ0=sQuery(id+"F0.wireOp",EDGE,"E122.MirrorCS");Q61=makeQuery(id+"F0.imprint","IMPRINT",FACE,{"disambiguationData":[TD([[makeQuery(id+"F0.imprint","IMPRINT",EDGE,{"derivedFrom":subQ0}),1.0]])]});}
            var Q62;
            {var subQ0=sQuery(id+"F0.wireOp",EDGE,"E124.MirrorCS");Q62=makeQuery(id+"F0.imprint","IMPRINT",FACE,{"disambiguationData":[TD([[makeQuery(id+"F0.imprint","IMPRINT",EDGE,{"derivedFrom":subQ0}),1.0]])]});}
            var Q63;
            {var subQ0=sQuery(id+"F0.wireOp",EDGE,"E126.MirrorCS");Q63=makeQuery(id+"F0.imprint","IMPRINT",FACE,{"disambiguationData":[TD([[makeQuery(id+"F0.imprint","IMPRINT",EDGE,{"derivedFrom":subQ0}),1.0]])]});}
            var Q64;
            {var subQ0=sQuery(id+"F0.wireOp",EDGE,"E128.MirrorCS");Q64=makeQuery(id+"F0.imprint","IMPRINT",FACE,{"disambiguationData":[TD([[makeQuery(id+"F0.imprint","IMPRINT",EDGE,{"derivedFrom":subQ0}),1.0]])]});}
            var Q65;
            {var subQ0=sQuery(id+"F0.wireOp",EDGE,"E130.MirrorCS");Q65=makeQuery(id+"F0.imprint","IMPRINT",FACE,{"disambiguationData":[TD([[makeQuery(id+"F0.imprint","IMPRINT",EDGE,{"derivedFrom":subQ0}),1.0]])]});}
            var Q66;
            {var subQ0=sQuery(id+"F0.wireOp",EDGE,"E132.MirrorCS");Q66=makeQuery(id+"F0.imprint","IMPRINT",FACE,{"disambiguationData":[TD([[makeQuery(id+"F0.imprint","IMPRINT",EDGE,{"derivedFrom":subQ0}),1.0]])]});}
            var Q67;
            {var subQ0=sQuery(id+"F0.wireOp",EDGE,"E134.MirrorCS");Q67=makeQuery(id+"F0.imprint","IMPRINT",FACE,{"disambiguationData":[TD([[makeQuery(id+"F0.imprint","IMPRINT",EDGE,{"derivedFrom":subQ0}),1.0]])]});}
            var Q68;
            {var subQ0=sQuery(id+"F0.wireOp",EDGE,"E136.MirrorCS");Q68=makeQuery(id+"F0.imprint","IMPRINT",FACE,{"disambiguationData":[TD([[makeQuery(id+"F0.imprint","IMPRINT",EDGE,{"derivedFrom":subQ0}),1.0]])]});}
            var Q69;
            {var subQ0=sQuery(id+"F0.wireOp",EDGE,"E138.MirrorCS");Q69=makeQuery(id+"F0.imprint","IMPRINT",FACE,{"disambiguationData":[TD([[makeQuery(id+"F0.imprint","IMPRINT",EDGE,{"derivedFrom":subQ0}),1.0]])]});}
            var Q70;
            {var subQ0=sQuery(id+"F0.wireOp",EDGE,"E140.MirrorCS");Q70=makeQuery(id+"F0.imprint","IMPRINT",FACE,{"disambiguationData":[TD([[makeQuery(id+"F0.imprint","IMPRINT",EDGE,{"derivedFrom":subQ0}),1.0]])]});}
            var Q71;
            {var subQ0=sQuery(id+"F0.wireOp",EDGE,"E142.MirrorCS");Q71=makeQuery(id+"F0.imprint","IMPRINT",FACE,{"disambiguationData":[TD([[makeQuery(id+"F0.imprint","IMPRINT",EDGE,{"derivedFrom":subQ0}),1.0]])]});}
            var Q72;
            {var subQ0=sQuery(id+"F0.wireOp",EDGE,"E144.MirrorCS");Q72=makeQuery(id+"F0.imprint","IMPRINT",FACE,{"disambiguationData":[TD([[makeQuery(id+"F0.imprint","IMPRINT",EDGE,{"derivedFrom":subQ0}),1.0]])]});}
            var Q73;
            {var subQ0=sQuery(id+"F0.wireOp",EDGE,"E146.MirrorCS");Q73=makeQuery(id+"F0.imprint","IMPRINT",FACE,{"disambiguationData":[TD([[makeQuery(id+"F0.imprint","IMPRINT",EDGE,{"derivedFrom":subQ0}),1.0]])]});}
            var Q74;
            {var subQ0=sQuery(id+"F0.wireOp",EDGE,"E150.MirrorCS");Q74=makeQuery(id+"F0.imprint","IMPRINT",FACE,{"disambiguationData":[TD([[makeQuery(id+"F0.imprint","IMPRINT",EDGE,{"derivedFrom":subQ0}),1.0]])]});}
            var Q75;
            {var subQ0=sQuery(id+"F0.wireOp",EDGE,"E152.MirrorCS");Q75=makeQuery(id+"F0.imprint","IMPRINT",FACE,{"disambiguationData":[TD([[makeQuery(id+"F0.imprint","IMPRINT",EDGE,{"derivedFrom":subQ0}),1.0]])]});}
            var Q76;
            {var subQ0=sQuery(id+"F0.wireOp",EDGE,"E148.MirrorCS");Q76=makeQuery(id+"F0.imprint","IMPRINT",FACE,{"disambiguationData":[TD([[makeQuery(id+"F0.imprint","IMPRINT",EDGE,{"derivedFrom":subQ0}),1.0]])]});}
            var Q77;
            {var subQ0=sQuery(id+"F0.wireOp",EDGE,"E154.MirrorCS");Q77=makeQuery(id+"F0.imprint","IMPRINT",FACE,{"disambiguationData":[TD([[makeQuery(id+"F0.imprint","IMPRINT",EDGE,{"derivedFrom":subQ0}),1.0]])]});}
            var Q78;
            {var subQ0=sQuery(id+"F0.wireOp",EDGE,"E156.MirrorCS");Q78=makeQuery(id+"F0.imprint","IMPRINT",FACE,{"disambiguationData":[TD([[makeQuery(id+"F0.imprint","IMPRINT",EDGE,{"derivedFrom":subQ0}),1.0]])]});}
            var Q79;
            {var subQ0=sQuery(id+"F0.wireOp",EDGE,"E158.MirrorCS");Q79=makeQuery(id+"F0.imprint","IMPRINT",FACE,{"disambiguationData":[TD([[makeQuery(id+"F0.imprint","IMPRINT",EDGE,{"derivedFrom":subQ0}),1.0]])]});}
            var Q80;
            {var subQ0=sQuery(id+"F0.wireOp",EDGE,"E160.MirrorCS");Q80=makeQuery(id+"F0.imprint","IMPRINT",FACE,{"disambiguationData":[TD([[makeQuery(id+"F0.imprint","IMPRINT",EDGE,{"derivedFrom":subQ0}),1.0]])]});}
            var Q81;
            {var subQ0=sQuery(id+"F0.wireOp",EDGE,"E162.MirrorCS");Q81=makeQuery(id+"F0.imprint","IMPRINT",FACE,{"disambiguationData":[TD([[makeQuery(id+"F0.imprint","IMPRINT",EDGE,{"derivedFrom":subQ0}),1.0]])]});}
            var Q82;
            {var subQ0=sQuery(id+"F0.wireOp",EDGE,"E164.MirrorCS");Q82=makeQuery(id+"F0.imprint","IMPRINT",FACE,{"disambiguationData":[TD([[makeQuery(id+"F0.imprint","IMPRINT",EDGE,{"derivedFrom":subQ0}),1.0]])]});}
            var Q83;
            {var subQ1=sQuery(id+"F0.wireOp",EDGE,"E0.right");Q83=makeQuery(id+"F0.imprint","IMPRINT",FACE,{"disambiguationData":[TD([[makeQuery(id+"F0.imprint","IMPRINT",EDGE,{"derivedFrom":subQ1}),-1.0]])]});}
            extrude(context, id + "F1", {"entities" : qUnion([Q0, Q1, Q2, Q3, Q4, Q5, Q6, Q7, Q8, Q9, Q10, Q11, Q12, Q13, Q14, Q15, Q16, Q17, Q18, Q19, Q20, Q21, Q22, Q23, Q24, Q25, Q26, Q27, Q28, Q29, Q30, Q31, Q32, Q33, Q34, Q35, Q36, Q37, Q38, Q39, Q40, Q41, Q42, Q43, Q44, Q45, Q46, Q47, Q48, Q49, Q50, Q51, Q52, Q53, Q54, Q55, Q56, Q57, Q58, Q59, Q60, Q61, Q62, Q63, Q64, Q65, Q66, Q67, Q68, Q69, Q70, Q71, Q72, Q73, Q74, Q75, Q76, Q77, Q78, Q79, Q80, Q81, Q82, Q83]), "depth" : 1.96 * mm, "offsetDistance" : 25 * mm});
        }
    });
